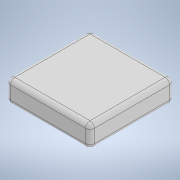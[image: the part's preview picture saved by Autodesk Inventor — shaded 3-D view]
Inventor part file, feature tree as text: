
AUTODESK INVENTOR PART (.ipt)
format: ipt  version: 2020 (Build 240168000, 168)  size: 115,712 bytes
history: native  units: mm
features: extrude x1, fillet x1, sketch x1
ambient origin geometry x8: Origin, YZ Plane, XZ Plane, XY Plane, X Axis, Y Axis, Z Axis, Center Point
bodies: Solid1 (feature_tree)
feature tree (3):
  extrude  "Extrusion1"  Depth=38.1mm
  fillet  "Fillet1"  Radius=10.0mm
  sketch  "Sketch1"  dims[d0=38.1mm d1=38.1mm d2=10.0mm d3=0.0mm d4=2.0mm d5=2.0mm]
